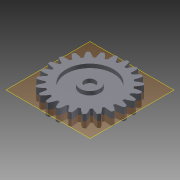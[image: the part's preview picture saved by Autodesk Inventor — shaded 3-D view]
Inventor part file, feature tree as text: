
AUTODESK INVENTOR PART (.ipt)
format: ipt  version: 2014 (Build 180170000, 170)  size: 258,560 bytes
history: native  units: mm (DEFAULTED — no unit token found)
features: plane x4, sketch x4, extrude x3, other x3, mirror x1
ambient origin geometry x8: Origin, YZ Plane, XZ Plane, XY Plane, X Axis, Y Axis, Z Axis, Center Point
bodies: Solid1 (feature_tree)
feature tree (15):
  extrude  "Extrusion1"  Depth=8.0mm TaperAngle=0.0deg
  plane  "Work Plane2"
  plane  "Work Plane8"
  plane  "Work Plane9"
  other  "Spur Gear"
  extrude  "Extrusion2"  Depth=10.0mm TaperAngle=0.0deg
  plane  "Work Plane11"
  mirror  "Mirror1"
  extrude  "Extrusion3"  Depth=1.36591mm TaperAngle=0.0deg
  sketch  "Sketch1"  dims[d0=50.0mm d1=8.0mm d2=0.0mm]
  sketch  "Sketch2"  dims[d3=46.0mm d4=10.0mm d5=0.0mm]
  other  "Srf1"
  sketch  "Sketch3"  dims[d16=66.0mm d17=0.0mm d34=1.36591mm]
  sketch  "Sketch4"  dims[d39=0.0mm d41=0.0mm d43=66.0mm d46=66.0mm d47=0.0mm d48=0.0mm d49=5.0mm d50=7.0mm d51=3.0mm d52=2.5mm d53=0.0mm d54=5.0mm d55=0.0mm]
  other  "Pitch Diameter"
